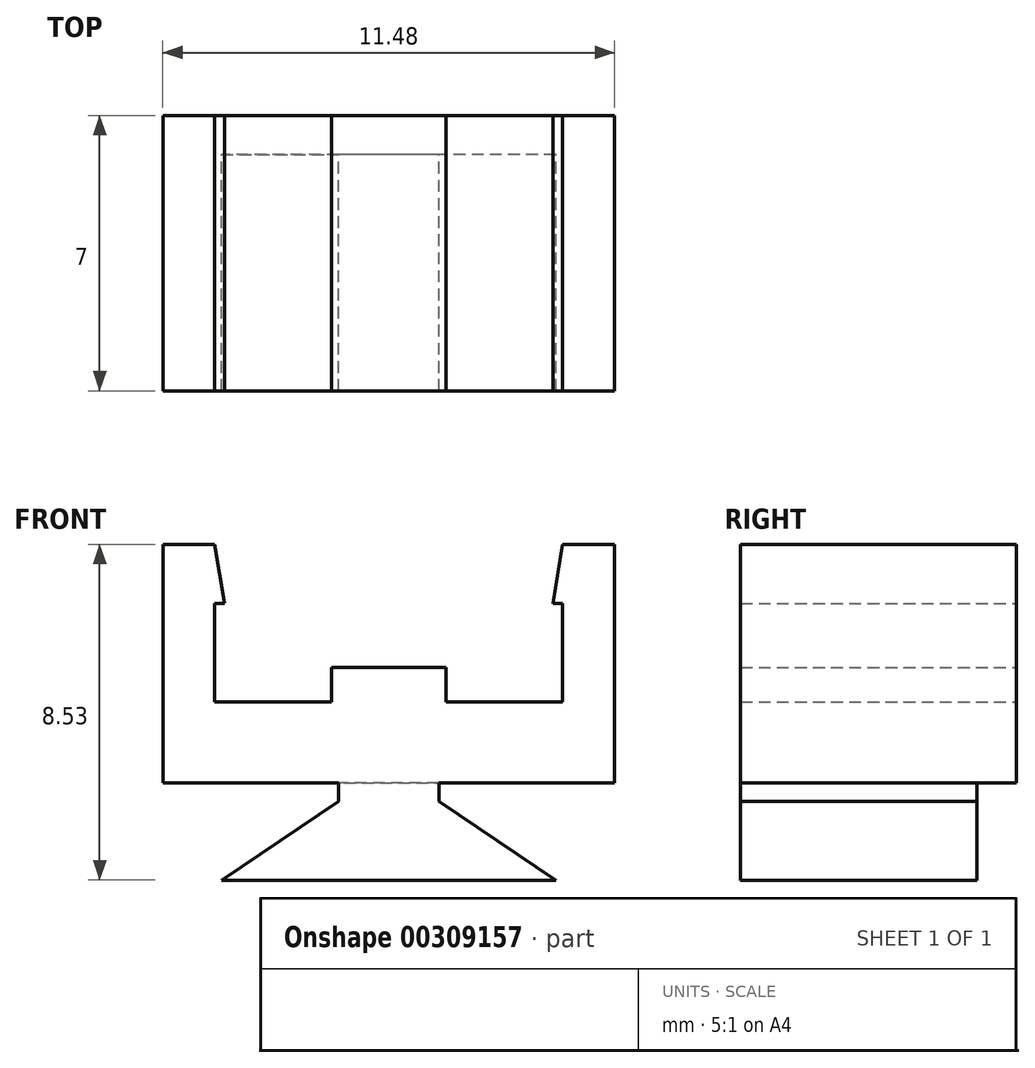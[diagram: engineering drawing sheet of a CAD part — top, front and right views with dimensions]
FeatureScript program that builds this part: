
annotation { "Feature Type Name" : "Feature", "Feature Type Description" : "" }
export const myFeature = defineFeature(function(context is Context, id is Id, definition is map)
    precondition{}
    {
        {
            var Q0;
            Q0=qCreatedBy(makeId("Front.planeOp"),FACE);
            var sketch = newSketch(context, id + "F0", { "sketchPlane" : qUnion([Q0])});
            skLineSegment(sketch, "E0", {"start": v(-3, 5) * mm, "end": v(0, 5) * mm});
            skLineSegment(sketch, "E1.MirrorCS", {"start": v(3, 5) * mm, "end": v(0, 5) * mm});
            skLineSegment(sketch, "E2", {"start": v(-1.45, 5) * mm, "end": v(-1.45, 5.89) * mm});
            skLineSegment(sketch, "E3", {"start": v(-1.45, 5.89) * mm, "end": v(0, 5.89) * mm});
            skLineSegment(sketch, "E4.MirrorCS", {"start": v(1.45, 5.89) * mm, "end": v(0, 5.89) * mm});
            skLineSegment(sketch, "E5.MirrorCS", {"start": v(1.45, 5) * mm, "end": v(1.45, 5.89) * mm});
            skLineSegment(sketch, "E6", {"start": v(4.42, 5) * mm, "end": v(4.42, 7.5) * mm});
            skLineSegment(sketch, "E7.MirrorCS", {"start": v(-4.42, 5) * mm, "end": v(-4.42, 7.5) * mm});
            skLineSegment(sketch, "E8", {"start": v(-4.42, 7.5) * mm, "end": v(-4.17, 7.5) * mm});
            skLineSegment(sketch, "E9", {"start": v(-4.42, 9) * mm, "end": v(-5.74, 9) * mm});
            skLineSegment(sketch, "E10", {"start": v(-5.74, 9) * mm, "end": v(-5.74, 2.96) * mm});
            skLineSegment(sketch, "E11.MirrorCS", {"start": v(4.42, 9) * mm, "end": v(5.74, 9) * mm});
            skLineSegment(sketch, "E12.MirrorCS", {"start": v(5.74, 9) * mm, "end": v(5.74, 2.96) * mm});
            skLineSegment(sketch, "E13.MirrorCS", {"start": v(4.42, 7.5) * mm, "end": v(4.17, 7.5) * mm});
            skLineSegment(sketch, "E14", {"start": v(-4.42, 5) * mm, "end": v(-3, 5) * mm});
            skLineSegment(sketch, "E15", {"start": v(3, 5) * mm, "end": v(4.42, 5) * mm});
            skPoint(sketch, "E16.end.orphan", {"position": v(-3.41, 9) * mm});
            skPoint(sketch, "E17.orphan", {"position": v(-3.41, 7.5) * mm});
            skPoint(sketch, "E18.MirrorCS.end.orphan", {"position": v(3.41, 9) * mm});
            skPoint(sketch, "E18.MirrorCS.start.orphan", {"position": v(3.41, 7.5) * mm});
            skPoint(sketch, "E19.end.orphan", {"position": v(-3.92, 9) * mm});
            skLineSegment(sketch, "E20", {"start": v(-4.42, 9) * mm, "end": v(-4.17, 7.5) * mm});
            skPoint(sketch, "E21.orphan", {"position": v(-3.92, 7.5) * mm});
            skLineSegment(sketch, "E22.MirrorCS", {"start": v(4.42, 9) * mm, "end": v(4.17, 7.5) * mm});
            skPoint(sketch, "E23.MirrorCS.end.orphan", {"position": v(3.92, 9) * mm});
            skPoint(sketch, "E24.MirrorCS.start.orphan", {"position": v(3.92, 7.5) * mm});
            skLineSegment(sketch, "E25", {"start": v(-5.74, 2.96) * mm, "end": v(-1.28, 2.96) * mm});
            skPoint(sketch, "E26.endSnap0", {"position": v(0, 2.96) * mm});
            skLineSegment(sketch, "E27", {"start": v(0, 0.48) * mm, "end": v(4.25, 0.48) * mm});
            skLineSegment(sketch, "E28", {"start": v(0, 0.48) * mm, "end": v(-4.25, 0.48) * mm});
            skLineSegment(sketch, "E29", {"start": v(-4.25, 0.48) * mm, "end": v(-1.28, 0.48) * mm, "construction": true});
            skLineSegment(sketch, "E30", {"start": v(-1.28, 2.48) * mm, "end": v(-1.28, 2.96) * mm});
            skLineSegment(sketch, "E31.MirrorCS", {"start": v(1.28, 2.48) * mm, "end": v(1.28, 2.96) * mm});
            skLineSegment(sketch, "E32", {"start": v(-4.25, 0.48) * mm, "end": v(-1.28, 2.48) * mm});
            skLineSegment(sketch, "E33.MirrorCS", {"start": v(4.25, 0.48) * mm, "end": v(1.28, 2.48) * mm});
            skLineSegment(sketch, "E34.trimOffspring", {"start": v(1.28, 2.96) * mm, "end": v(5.74, 2.96) * mm});
            skPoint(sketch, "E35.orphan", {"position": v(1.28, 0.48) * mm});
            skPoint(sketch, "E26.start.orphan", {"position": v(0, 2.96) * mm});
            skSolve(sketch);
        }
        {
            var Q0;
            Q0 = qSketchRegion(id + "F0", true);
            extrude(context, id + "F1", {"entities" : qUnion([Q0]), "depth" : 7 * mm});
        }
        {
            var Q0;
            Q0=makeQuery(id+"F1.opExtrude","CAP_FACE",FACE,{"disambiguationData":[OSD([sQuery(id+"F0.wireOp",EDGE,"E0"),sQuery(id+"F0.wireOp",EDGE,"E1.MirrorCS"),sQuery(id+"F0.wireOp",EDGE,"E2"),sQuery(id+"F0.wireOp",EDGE,"E3"),sQuery(id+"F0.wireOp",EDGE,"E4.MirrorCS"),sQuery(id+"F0.wireOp",EDGE,"E5.MirrorCS"),sQuery(id+"F0.wireOp",EDGE,"E7.MirrorCS"),sQuery(id+"F0.wireOp",EDGE,"E8"),sQuery(id+"F0.wireOp",EDGE,"E9"),sQuery(id+"F0.wireOp",EDGE,"E10"),sQuery(id+"F0.wireOp",EDGE,"E11.MirrorCS"),sQuery(id+"F0.wireOp",EDGE,"E12.MirrorCS"),sQuery(id+"F0.wireOp",EDGE,"E6"),sQuery(id+"F0.wireOp",EDGE,"E13.MirrorCS"),sQuery(id+"F0.wireOp",EDGE,"E14"),sQuery(id+"F0.wireOp",EDGE,"E15"),sQuery(id+"F0.wireOp",EDGE,"E20"),sQuery(id+"F0.wireOp",EDGE,"E22.MirrorCS"),sQuery(id+"F0.wireOp",EDGE,"E25"),sQuery(id+"F0.wireOp",EDGE,"E27"),sQuery(id+"F0.wireOp",EDGE,"E28"),sQuery(id+"F0.wireOp",EDGE,"E30"),sQuery(id+"F0.wireOp",EDGE,"E31.MirrorCS"),sQuery(id+"F0.wireOp",EDGE,"E32"),sQuery(id+"F0.wireOp",EDGE,"E33.MirrorCS"),sQuery(id+"F0.wireOp",EDGE,"E34.trimOffspring")])],"isStart":true});
            var sketch = newSketch(context, id + "F2", { "sketchPlane" : qUnion([Q0])});
            skLineSegment(sketch, "E36", {"start": v(-1.28, 2.96) * mm, "end": v(1.28, 2.96) * mm});
            skSolve(sketch);
        }
        {
            var Q0;
            Q0 = qSketchRegion(id + "F2", true);
            var Q1;
            Q1=makeQuery(id+"F2.imprint","IMPRINT",FACE,{"disambiguationData":[TD([[makeQuery(id+"F2.imprint","IMPRINT",EDGE,{"derivedFrom":sQuery(id+"F2.wireOp",EDGE,"E36")}),-1.0]])]});
            extrude(context, id + "F3", {"entities" : qUnion([Q0, Q1]), "operationType" : NewBodyOperationType.REMOVE, "oppositeDirection" : true, "depth" : 1 * mm});
        }
    });
